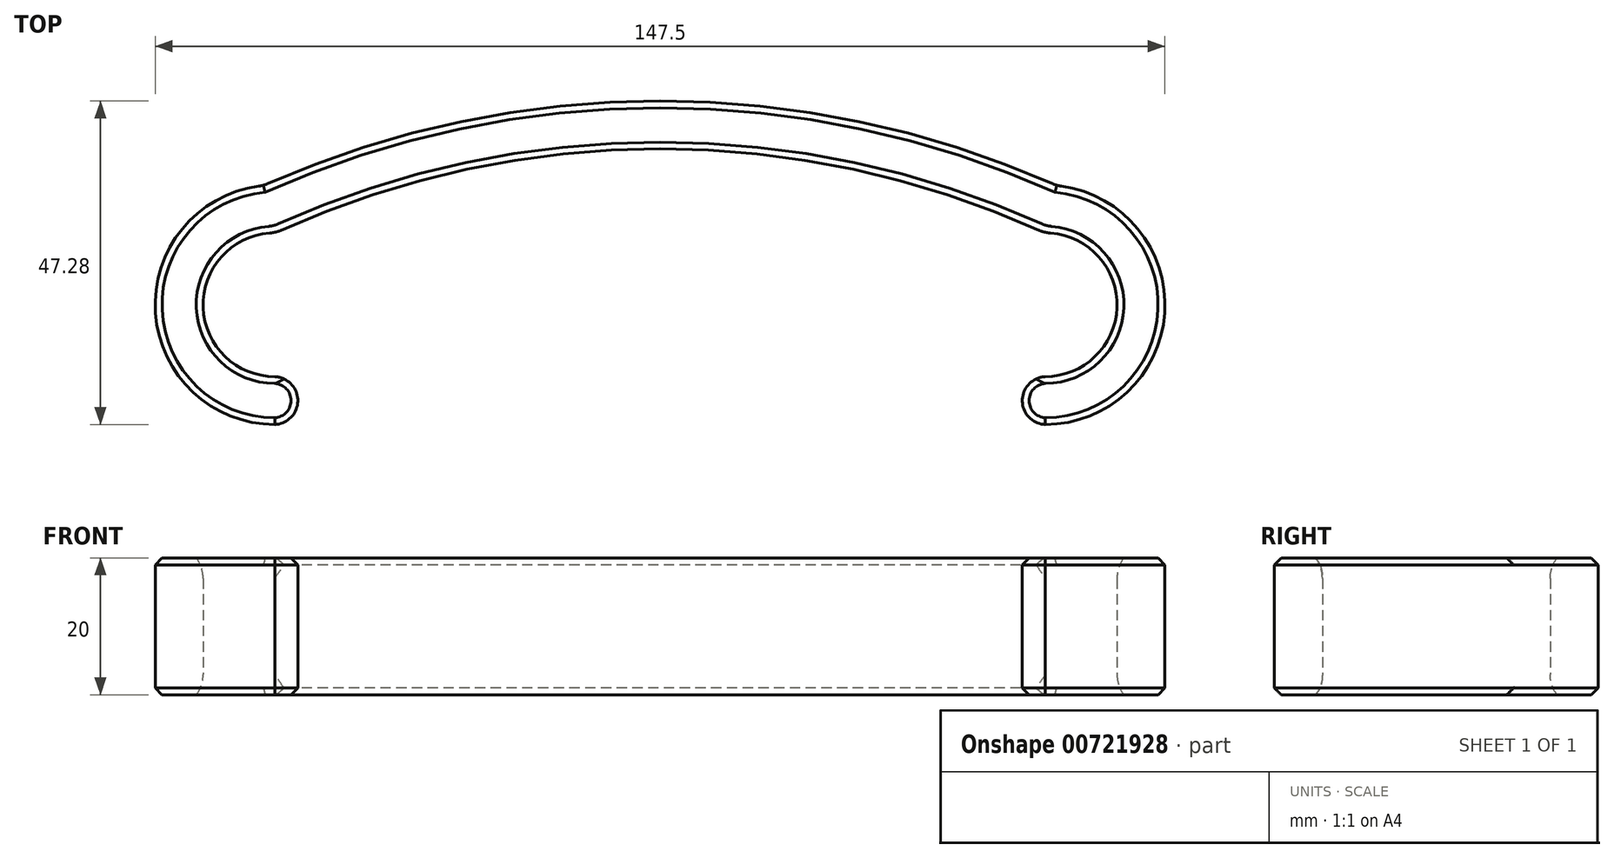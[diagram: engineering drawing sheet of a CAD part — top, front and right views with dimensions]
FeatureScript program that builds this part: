
annotation { "Feature Type Name" : "Feature", "Feature Type Description" : "" }
export const myFeature = defineFeature(function(context is Context, id is Id, definition is map)
    precondition{}
    {
        {
            var Q0;
            Q0=qCreatedBy(makeId("Top.planeOp"),FACE);
            var sketch = newSketch(context, id + "F0", { "sketchPlane" : qUnion([Q0])});
            skArc(sketch, "E0", {"start": v(-56.25, 10.5) * mm, "mid": v(-66.75, 0) * mm, "end": v(-56.25, -10.5) * mm});
            skArc(sketch, "E1.0", {"start": v(-57.94, 17.42) * mm, "mid": v(-73.73, -0.85) * mm, "end": v(-56.25, -17.5) * mm});
            skArc(sketch, "E2", {"start": v(-56.25, -17.5) * mm, "mid": v(-52.91, -14) * mm, "end": v(-56.25, -10.5) * mm});
            skLineSegment(sketch, "E3", {"start": v(0, 0) * mm, "end": v(0, 51.47) * mm, "construction": true});
            skArc(sketch, "E4.MirrorCS", {"start": v(56.25, -17.5) * mm, "mid": v(52.91, -14) * mm, "end": v(56.25, -10.5) * mm});
            skArc(sketch, "E5.MirrorCS", {"start": v(56.25, 10.5) * mm, "mid": v(66.75, 0) * mm, "end": v(56.25, -10.5) * mm});
            skArc(sketch, "E6.MirrorCS", {"start": v(57.94, 17.42) * mm, "mid": v(73.73, -0.85) * mm, "end": v(56.25, -17.5) * mm});
            skArc(sketch, "E7", {"start": v(56.25, 10.5) * mm, "mid": v(0, 22.78) * mm, "end": v(-56.25, 10.5) * mm});
            skArc(sketch, "E8.0", {"start": v(57.94, 17.42) * mm, "mid": v(0, 29.78) * mm, "end": v(-57.94, 17.42) * mm});
            skSolve(sketch);
        }
        {
            var Q0;
            Q0=makeQuery(id+"F0.imprint","IMPRINT",FACE,{"disambiguationData":[TD([[makeQuery(id+"F0.imprint","IMPRINT",EDGE,{"derivedFrom":sQuery(id+"F0.wireOp",EDGE,"E0")}),-1.0]])]});
            extrude(context, id + "F1", {"entities" : qUnion([Q0]), "depth" : 20 * mm, "offsetDistance" : 25 * mm});
        }
        {
            var Q0;
            Q0=makeQuery(id+"F1.opExtrude","CAP_FACE",FACE,{"disambiguationData":[OSD([sQuery(id+"F0.wireOp",EDGE,"E0"),sQuery(id+"F0.wireOp",EDGE,"E1.0"),sQuery(id+"F0.wireOp",EDGE,"E2"),sQuery(id+"F0.wireOp",EDGE,"E4.MirrorCS"),sQuery(id+"F0.wireOp",EDGE,"E5.MirrorCS"),sQuery(id+"F0.wireOp",EDGE,"E6.MirrorCS"),sQuery(id+"F0.wireOp",EDGE,"E7"),sQuery(id+"F0.wireOp",EDGE,"E8.0")])],"isStart":true});
            var Q1;
            Q1=makeQuery(id+"F1.opExtrude","CAP_FACE",FACE,{"disambiguationData":[OSD([sQuery(id+"F0.wireOp",EDGE,"E0"),sQuery(id+"F0.wireOp",EDGE,"E1.0"),sQuery(id+"F0.wireOp",EDGE,"E2"),sQuery(id+"F0.wireOp",EDGE,"E4.MirrorCS"),sQuery(id+"F0.wireOp",EDGE,"E5.MirrorCS"),sQuery(id+"F0.wireOp",EDGE,"E6.MirrorCS"),sQuery(id+"F0.wireOp",EDGE,"E7"),sQuery(id+"F0.wireOp",EDGE,"E8.0")])],"isStart":false});
            chamfer(context, id + "F2", {"entities" : qUnion([Q0, Q1]), "width" : 1 * mm, "tangentPropagation" : true});
        }
        {
            var Q0;
            {var subQ0=sQuery(id+"F0.wireOp",EDGE,"E7");Q0=makeQuery(id+"F2.opChamfer","BLEND_EDGE",EDGE,{"blendedFrom":[makeQuery(id+"F1.opExtrude","CAP_EDGE",EDGE,{"disambiguationData":[OSD([subQ0])],"isStart":false}),makeQuery(id+"F1.opExtrude","SWEPT_FACE",FACE,{"disambiguationData":[OSD([subQ0])]})],"blendedInto":[makeQuery(id+"F1.opExtrude","SWEPT_FACE",FACE,{"disambiguationData":[OSD([subQ0])]})]});}
            var Q1;
            {var subQ0=sQuery(id+"F0.wireOp",EDGE,"E7");Q1=makeQuery(id+"F2.opChamfer","BLEND_EDGE",EDGE,{"blendedFrom":[makeQuery(id+"F1.opExtrude","CAP_EDGE",EDGE,{"disambiguationData":[OSD([subQ0])],"isStart":true}),makeQuery(id+"F1.opExtrude","SWEPT_FACE",FACE,{"disambiguationData":[OSD([subQ0])]})],"blendedInto":[makeQuery(id+"F1.opExtrude","SWEPT_FACE",FACE,{"disambiguationData":[OSD([subQ0])]})]});}
            var Q2;
            {var subQ0=sQuery(id+"F0.wireOp",EDGE,"E0");Q2=makeQuery(id+"F2.opChamfer","BLEND_EDGE",EDGE,{"blendedFrom":[makeQuery(id+"F1.opExtrude","CAP_EDGE",EDGE,{"disambiguationData":[OSD([subQ0])],"isStart":false}),makeQuery(id+"F1.opExtrude","SWEPT_FACE",FACE,{"disambiguationData":[OSD([subQ0])]})],"blendedInto":[makeQuery(id+"F1.opExtrude","SWEPT_FACE",FACE,{"disambiguationData":[OSD([subQ0])]})]});}
            var Q3;
            {var subQ0=sQuery(id+"F0.wireOp",EDGE,"E0");Q3=makeQuery(id+"F2.opChamfer","BLEND_EDGE",EDGE,{"blendedFrom":[makeQuery(id+"F1.opExtrude","CAP_EDGE",EDGE,{"disambiguationData":[OSD([subQ0])],"isStart":true}),makeQuery(id+"F1.opExtrude","SWEPT_FACE",FACE,{"disambiguationData":[OSD([subQ0])]})],"blendedInto":[makeQuery(id+"F1.opExtrude","SWEPT_FACE",FACE,{"disambiguationData":[OSD([subQ0])]})]});}
            var Q4;
            {var subQ0=sQuery(id+"F0.wireOp",EDGE,"E5.MirrorCS");Q4=makeQuery(id+"F2.opChamfer","BLEND_EDGE",EDGE,{"blendedFrom":[makeQuery(id+"F1.opExtrude","CAP_EDGE",EDGE,{"disambiguationData":[OSD([subQ0])],"isStart":true}),makeQuery(id+"F1.opExtrude","SWEPT_FACE",FACE,{"disambiguationData":[OSD([subQ0])]})],"blendedInto":[makeQuery(id+"F1.opExtrude","SWEPT_FACE",FACE,{"disambiguationData":[OSD([subQ0])]})]});}
            var Q5;
            {var subQ0=sQuery(id+"F0.wireOp",EDGE,"E5.MirrorCS");Q5=makeQuery(id+"F2.opChamfer","BLEND_EDGE",EDGE,{"blendedFrom":[makeQuery(id+"F1.opExtrude","CAP_EDGE",EDGE,{"disambiguationData":[OSD([subQ0])],"isStart":false}),makeQuery(id+"F1.opExtrude","SWEPT_FACE",FACE,{"disambiguationData":[OSD([subQ0])]})],"blendedInto":[makeQuery(id+"F1.opExtrude","SWEPT_FACE",FACE,{"disambiguationData":[OSD([subQ0])]})]});}
            var Q6;
            Q6=makeQuery(id+"F1.opExtrude","SWEPT_EDGE",EDGE,{"disambiguationData":[OSD([sQuery(id+"F0.wireOp",EDGE,"E6.MirrorCS"),sQuery(id+"F0.wireOp",EDGE,"E8.0")])]});
            var Q7;
            Q7=makeQuery(id+"F1.opExtrude","SWEPT_EDGE",EDGE,{"disambiguationData":[OSD([sQuery(id+"F0.wireOp",EDGE,"E1.0"),sQuery(id+"F0.wireOp",EDGE,"E8.0")])]});
            fillet(context, id + "F3", {"entities" : qUnion([Q0, Q1, Q2, Q3, Q4, Q5, Q6, Q7]), "tangentPropagation" : true, "radius" : 5 * mm, "defaultsChanged" : false, "vertexSettings" : [], "allowEdgeOverflow" : false});
        }
        {
            var Q0;
            Q0=makeQuery(id+"F1.opExtrude","SWEPT_EDGE",EDGE,{"disambiguationData":[OSD([sQuery(id+"F0.wireOp",EDGE,"E0"),sQuery(id+"F0.wireOp",EDGE,"E7")])]});
            var Q1;
            Q1=makeQuery(id+"F1.opExtrude","SWEPT_EDGE",EDGE,{"disambiguationData":[OSD([sQuery(id+"F0.wireOp",EDGE,"E5.MirrorCS"),sQuery(id+"F0.wireOp",EDGE,"E7")])]});
            fillet(context, id + "F4", {"entities" : qUnion([Q0, Q1]), "tangentPropagation" : true, "radius" : 5 * mm, "defaultsChanged" : true, "vertexSettings" : [], "allowEdgeOverflow" : false});
        }
    });
